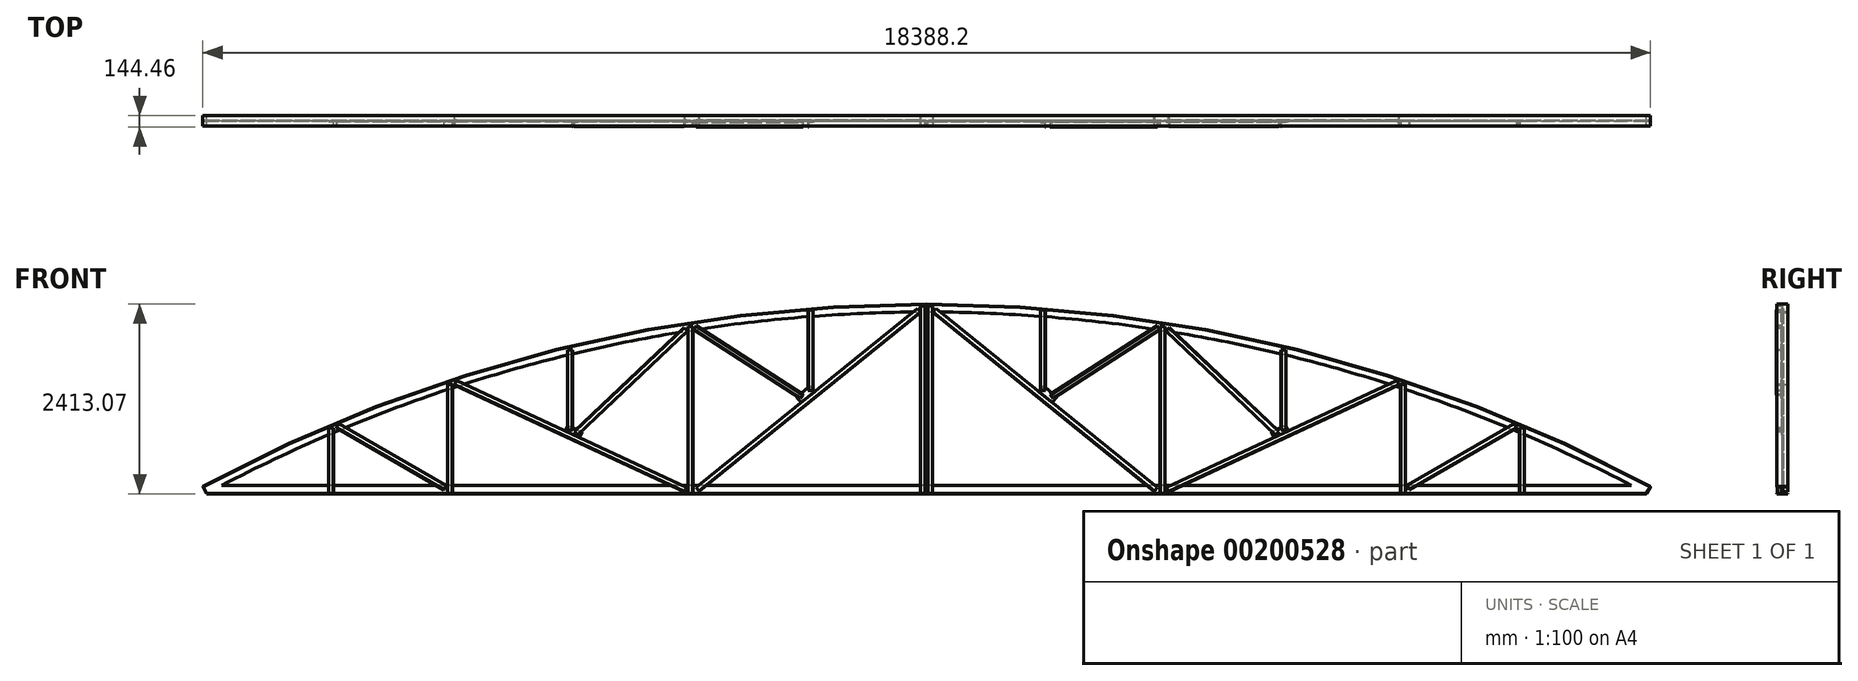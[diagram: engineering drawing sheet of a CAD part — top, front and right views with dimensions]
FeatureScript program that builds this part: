
annotation { "Feature Type Name" : "Feature", "Feature Type Description" : "" }
export const myFeature = defineFeature(function(context is Context, id is Id, definition is map)
    precondition{}
    {
        {
            var Q0;
            Q0=qCreatedBy(makeId("Front.planeOp"),FACE);
            var sketch = newSketch(context, id + "F0", { "sketchPlane" : qUnion([Q0])});
            skLineSegment(sketch, "E0", {"start": v(0, 0) * mm, "end": v(18288, 0) * mm});
            skArc(sketch, "E1", {"start": v(18288, 0) * mm, "mid": v(9144, 2305.05) * mm, "end": v(0, 0) * mm});
            skLineSegment(sketch, "E2", {"start": v(1612.9, 0) * mm, "end": v(1612.9, 774.13) * mm});
            skLineSegment(sketch, "E3", {"start": v(3092.45, 0) * mm, "end": v(3092.45, 1331.2) * mm});
            skLineSegment(sketch, "E4", {"start": v(6115.05, 0) * mm, "end": v(6115.05, 2065.75) * mm});
            skLineSegment(sketch, "E5", {"start": v(9144, 0) * mm, "end": v(9144, 2305.05) * mm});
            skLineSegment(sketch, "E6", {"start": v(7629.52, 1223.6) * mm, "end": v(7629.52, 2245.5) * mm});
            skLineSegment(sketch, "E7", {"start": v(3092.45, 0) * mm, "end": v(1692.88, 807.83) * mm});
            skLineSegment(sketch, "E8", {"start": v(6115.05, 0) * mm, "end": v(3187.59, 1362.37) * mm});
            skLineSegment(sketch, "E9", {"start": v(4651.32, 681.18) * mm, "end": v(4651.32, 1774.56) * mm});
            skLineSegment(sketch, "E10", {"start": v(4651.32, 681.18) * mm, "end": v(6115.05, 2065.75) * mm});
            skLineSegment(sketch, "E11", {"start": v(6190.76, 2077.64) * mm, "end": v(7580.54, 1184.02) * mm});
            skLineSegment(sketch, "E12.MirrorCS", {"start": v(12172.95, 0) * mm, "end": v(9144, 2305.05) * mm});
            skLineSegment(sketch, "E13.MirrorCS", {"start": v(10658.47, 1152.53) * mm, "end": v(10658.47, 2245.5) * mm});
            skLineSegment(sketch, "E14.MirrorCS", {"start": v(12097.24, 2077.64) * mm, "end": v(10658.47, 1152.52) * mm});
            skLineSegment(sketch, "E15.MirrorCS", {"start": v(12172.95, 0) * mm, "end": v(12172.95, 2065.75) * mm});
            skLineSegment(sketch, "E16.MirrorCS", {"start": v(13636.68, 681.18) * mm, "end": v(12172.95, 2065.75) * mm});
            skLineSegment(sketch, "E17.MirrorCS", {"start": v(13636.68, 681.18) * mm, "end": v(13636.68, 1774.56) * mm});
            skLineSegment(sketch, "E18.MirrorCS", {"start": v(12172.95, 0) * mm, "end": v(15100.41, 1362.37) * mm});
            skLineSegment(sketch, "E19.MirrorCS", {"start": v(15195.55, 0) * mm, "end": v(15195.55, 1331.2) * mm});
            skLineSegment(sketch, "E20.MirrorCS", {"start": v(15195.55, 0) * mm, "end": v(16595.12, 807.83) * mm});
            skLineSegment(sketch, "E21.MirrorCS", {"start": v(16675.1, 0) * mm, "end": v(16675.1, 774.13) * mm});
            skLineSegment(sketch, "E22", {"start": v(6115.05, 0) * mm, "end": v(8967.06, 2304.24) * mm});
            skPoint(sketch, "E23.end.orphan", {"position": v(7629.52, 1152.53) * mm});
            skSolve(sketch);
        }
        {
            var Q0;
            Q0=qCreatedBy(makeId("Right.planeOp"),FACE);
            var sketch = newSketch(context, id + "F1", { "sketchPlane" : qUnion([Q0])});
            skLineSegment(sketch, "E24.bottom", {"start": v(-68.26, -3.18) * mm, "end": v(68.26, -3.18) * mm});
            skLineSegment(sketch, "E24.top", {"start": v(-68.26, 3.18) * mm, "end": v(-3.17, 3.18) * mm});
            skLineSegment(sketch, "E24.left", {"start": v(-68.26, -3.18) * mm, "end": v(-68.26, 3.18) * mm});
            skLineSegment(sketch, "E24.right", {"start": v(68.26, -3.18) * mm, "end": v(68.26, 3.18) * mm});
            skPoint(sketch, "E24.middle", {"position": v(0, 0) * mm});
            skLineSegment(sketch, "E25.top", {"start": v(-3.18, 104.78) * mm, "end": v(3.17, 104.78) * mm});
            skLineSegment(sketch, "E25.left", {"start": v(-3.17, 3.18) * mm, "end": v(-3.18, 104.78) * mm});
            skLineSegment(sketch, "E25.right", {"start": v(3.18, 3.18) * mm, "end": v(3.17, 104.78) * mm});
            skLineSegment(sketch, "E26.trimOffspring", {"start": v(3.17, 3.18) * mm, "end": v(68.26, 3.18) * mm});
            skSolve(sketch);
        }
        {
            var Q0;
            Q0 = qSketchRegion(id + "F1", true);
            var Q1;
            Q1=sQuery(id+"F0.wireOp",VERTEX,"E1.start");
            extrude(context, id + "F2", {"entities" : qUnion([Q0]), "endBound" : BoundingType.UP_TO_VERTEX, "endBoundEntityVertex" : qUnion([Q1]), "depth" : 25.4 * mm});
        }
        {
            var Q0;
            Q0=sQuery(id+"F0.wireOp",EDGE,"E1");
            var Q1;
            Q1=sQuery(id+"F0.wireOp",VERTEX,"E0.start");
            cPlane(context, id + "F3", {"entities" : qUnion([Q0, Q1]), "cplaneType" : CPlaneType.CURVE_POINT, "offset" : 25.4 * mm, "width" : 152.4 * mm, "height" : 152.4 * mm});
        }
        {
            var Q0;
            Q0=qCreatedBy(id+"F3.planeOp",FACE);
            var sketch = newSketch(context, id + "F4", { "sketchPlane" : qUnion([Q0])});
            skPoint(sketch, "E27.middle", {"position": v(0, 0) * mm});
            skLineSegment(sketch, "E28.left", {"start": v(3.18, 3.25) * mm, "end": v(3.17, 98.5) * mm});
            skLineSegment(sketch, "E28.right", {"start": v(-3.17, 3.25) * mm, "end": v(-3.18, 98.5) * mm});
            skLineSegment(sketch, "E29", {"start": v(-3.17, 3.25) * mm, "end": v(3.18, 3.25) * mm});
            skLineSegment(sketch, "E30", {"start": v(68.26, 104.85) * mm, "end": v(68.26, 98.5) * mm});
            skLineSegment(sketch, "E31", {"start": v(68.26, 98.5) * mm, "end": v(3.17, 98.5) * mm});
            skLineSegment(sketch, "E32", {"start": v(-68.26, 104.85) * mm, "end": v(-68.26, 98.5) * mm});
            skLineSegment(sketch, "E33", {"start": v(-68.26, 98.5) * mm, "end": v(-3.18, 98.5) * mm});
            skPoint(sketch, "E34.0", {"position": v(68.26, -2.8) * mm});
            skPoint(sketch, "E34.1", {"position": v(-68.26, -2.8) * mm});
            skLineSegment(sketch, "E35", {"start": v(-68.26, 104.85) * mm, "end": v(68.26, 104.85) * mm});
            skSolve(sketch);
        }
        {
            var Q0;
            Q0=makeQuery(id+"F4.imprint","IMPRINT",FACE,{"disambiguationData":[TD([[makeQuery(id+"F4.imprint","IMPRINT",EDGE,{"derivedFrom":sQuery(id+"F4.wireOp",EDGE,"E28.left")}),1.0]])]});
            var Q1;
            Q1=sQuery(id+"F0.wireOp",EDGE,"E1");
            sweep(context, id + "F5", {"profiles" : qUnion([Q0]), "path" : qUnion([Q1])});
        }
        {
            var Q0;
            Q0=sQuery(id+"F0.wireOp",EDGE,"E2");
            var Q1;
            Q1=sQuery(id+"F0.wireOp",VERTEX,"E2.start");
            cPlane(context, id + "F6", {"entities" : qUnion([Q0, Q1]), "cplaneType" : CPlaneType.CURVE_POINT, "offset" : 25.4 * mm, "width" : 152.4 * mm, "height" : 152.4 * mm});
        }
        {
            var Q0;
            Q0=qCreatedBy(id+"F6.planeOp",FACE);
            var sketch = newSketch(context, id + "F7", { "sketchPlane" : qUnion([Q0])});
            skLineSegment(sketch, "E36", {"start": v(1612.9, -66.68) * mm, "end": v(1606.55, -66.68) * mm});
            skLineSegment(sketch, "E37", {"start": v(1606.55, -66.68) * mm, "end": v(1606.55, -9.53) * mm});
            skPoint(sketch, "E38.bottom.start.orphan", {"position": v(1606.55, 0) * mm});
            skLineSegment(sketch, "E39", {"start": v(1612.9, -3.17) * mm, "end": v(1612.9, -66.68) * mm});
            skPoint(sketch, "E40.0", {"position": v(1612.9, 0) * mm});
            skLineSegment(sketch, "E41", {"start": v(1606.55, -9.53) * mm, "end": v(1549.4, -9.53) * mm});
            skLineSegment(sketch, "E42", {"start": v(1549.4, 0) * mm, "end": v(1612.9, 0) * mm});
            skLineSegment(sketch, "E43", {"start": v(1549.4, -3.18) * mm, "end": v(1612.9, -3.17) * mm});
            skPoint(sketch, "E44.start.orphan", {"position": v(1549.4, -6.35) * mm});
            skLineSegment(sketch, "E45", {"start": v(1549.4, -9.53) * mm, "end": v(1549.4, -3.18) * mm});
            skSolve(sketch);
        }
        {
            var Q0;
            Q0 = qSketchRegion(id + "F7", true);
            extrude(context, id + "F8", {"entities" : qUnion([Q0]), "operationType" : NewBodyOperationType.ADD, "depth" : 838.2 * mm});
        }
        {
            var Q0;
            Q0=sQuery(id+"F0.wireOp",EDGE,"E7");
            var Q1;
            Q1=sQuery(id+"F0.wireOp",VERTEX,"E3.start");
            cPlane(context, id + "F9", {"entities" : qUnion([Q0, Q1]), "cplaneType" : CPlaneType.CURVE_POINT, "offset" : 25.4 * mm, "width" : 152.4 * mm, "height" : 152.4 * mm});
        }
        {
            var Q0;
            Q0=qCreatedBy(id+"F9.planeOp",FACE);
            var sketch = newSketch(context, id + "F10", { "sketchPlane" : qUnion([Q0])});
            skPoint(sketch, "E46.0", {"position": v(2.83, 1546.43) * mm});
            skLineSegment(sketch, "E47", {"start": v(3.18, 1545.92) * mm, "end": v(66.67, 1545.92) * mm});
            skLineSegment(sketch, "E48", {"start": v(66.67, 1545.92) * mm, "end": v(66.67, 1552.27) * mm});
            skLineSegment(sketch, "E49", {"start": v(66.67, 1552.27) * mm, "end": v(9.52, 1552.27) * mm});
            skLineSegment(sketch, "E50", {"start": v(9.52, 1552.27) * mm, "end": v(9.52, 1609.42) * mm});
            skLineSegment(sketch, "E51", {"start": v(9.52, 1609.42) * mm, "end": v(3.17, 1609.42) * mm});
            skLineSegment(sketch, "E52", {"start": v(3.17, 1609.42) * mm, "end": v(3.17, 1545.92) * mm});
            skSolve(sketch);
        }
        {
            var Q0;
            Q0 = qSketchRegion(id + "F10", true);
            extrude(context, id + "F11", {"entities" : qUnion([Q0]), "depth" : 1574.8 * mm});
        }
        {
            var Q0;
            Q0=sQuery(id+"F0.wireOp",EDGE,"E3");
            var Q1;
            Q1=sQuery(id+"F0.wireOp",VERTEX,"E7.start");
            cPlane(context, id + "F12", {"entities" : qUnion([Q0, Q1]), "cplaneType" : CPlaneType.CURVE_POINT, "offset" : 25.4 * mm, "width" : 152.4 * mm, "height" : 152.4 * mm});
        }
        {
            var Q0;
            Q0=qCreatedBy(id+"F12.planeOp",FACE);
            var sketch = newSketch(context, id + "F13", { "sketchPlane" : qUnion([Q0])});
            skLineSegment(sketch, "E53", {"start": v(3124.65, -66.68) * mm, "end": v(3124.65, -9.53) * mm});
            skLineSegment(sketch, "E54", {"start": v(3124.65, -66.67) * mm, "end": v(3118.3, -66.67) * mm});
            skLineSegment(sketch, "E55", {"start": v(3118.3, -9.53) * mm, "end": v(3118.3, -66.67) * mm});
            skLineSegment(sketch, "E56", {"start": v(3118.3, -3.17) * mm, "end": v(3061.15, -3.18) * mm});
            skLineSegment(sketch, "E57", {"start": v(3061.15, -3.18) * mm, "end": v(3061.15, -9.53) * mm});
            skLineSegment(sketch, "E58", {"start": v(3061.15, -9.53) * mm, "end": v(3118.3, -9.53) * mm});
            skLineSegment(sketch, "E59", {"start": v(3124.65, -9.53) * mm, "end": v(3124.65, -3.17) * mm});
            skLineSegment(sketch, "E60", {"start": v(3124.65, -3.17) * mm, "end": v(3118.3, -3.17) * mm});
            skSolve(sketch);
        }
        {
            var Q0;
            Q0 = qSketchRegion(id + "F13", true);
            extrude(context, id + "F14", {"entities" : qUnion([Q0]), "depth" : 1386.84 * mm});
        }
        {
            var Q0;
            Q0=makeQuery(id+"F11.opExtrude","SWEPT_BODY",BODY,{"disambiguationData":[OSD([sQuery(id+"F10.wireOp",EDGE,"E47"),sQuery(id+"F10.wireOp",EDGE,"E48"),sQuery(id+"F10.wireOp",EDGE,"E49"),sQuery(id+"F10.wireOp",EDGE,"E50"),sQuery(id+"F10.wireOp",EDGE,"E51"),sQuery(id+"F10.wireOp",EDGE,"E52")])]});
            var Q1;
            Q1=sQuery(id+"F0.wireOp",EDGE,"E7");
            var Q2;
            Q2=sQuery(id+"F0.wireOp",EDGE,"E7");
            transform(context, id + "F15", {"entities" : qUnion([Q0]), "transformType" : TransformType.TRANSLATION_DISTANCE, "transformDirection" : qUnion([Q2]), "distance" : 95.25 * mm, "makeCopy" : false});
        }
        {
            var Q0;
            Q0=sQuery(id+"F0.wireOp",EDGE,"E8");
            var Q1;
            Q1=sQuery(id+"F0.wireOp",VERTEX,"E8.start");
            cPlane(context, id + "F16", {"entities" : qUnion([Q0, Q1]), "cplaneType" : CPlaneType.CURVE_POINT, "offset" : 25.4 * mm, "width" : 152.4 * mm, "height" : 152.4 * mm});
        }
        {
            var Q0;
            Q0=qCreatedBy(id+"F16.planeOp",FACE);
            cPlane(context, id + "F17", {"entities" : qUnion([Q0]), "cplaneType" : CPlaneType.OFFSET, "offset" : 50.8 * mm, "width" : 152.4 * mm, "height" : 152.4 * mm});
        }
        {
            var Q0;
            Q0=qCreatedBy(id+"F17.planeOp",FACE);
            var sketch = newSketch(context, id + "F18", { "sketchPlane" : qUnion([Q0])});
            skPoint(sketch, "E61.0", {"position": v(0, 2580.09) * mm});
            skLineSegment(sketch, "E62.MirrorCS", {"start": v(-3.18, 2580.09) * mm, "end": v(-3.18, 2643.59) * mm});
            skLineSegment(sketch, "E63.MirrorCS", {"start": v(-3.18, 2643.59) * mm, "end": v(-9.53, 2643.59) * mm});
            skLineSegment(sketch, "E64.MirrorCS", {"start": v(-9.53, 2643.59) * mm, "end": v(-9.53, 2586.44) * mm});
            skLineSegment(sketch, "E65.MirrorCS", {"start": v(-9.53, 2586.44) * mm, "end": v(-66.67, 2586.44) * mm});
            skLineSegment(sketch, "E66.MirrorCS", {"start": v(-66.67, 2586.44) * mm, "end": v(-66.67, 2580.09) * mm});
            skLineSegment(sketch, "E67.MirrorCS", {"start": v(-66.67, 2580.09) * mm, "end": v(-3.18, 2580.09) * mm});
            skLineSegment(sketch, "E68.MirrorCS", {"start": v(3.18, 2643.59) * mm, "end": v(9.53, 2643.59) * mm});
            skLineSegment(sketch, "E69.MirrorCS", {"start": v(66.67, 2586.44) * mm, "end": v(66.67, 2580.09) * mm});
            skLineSegment(sketch, "E70.MirrorCS", {"start": v(66.67, 2580.09) * mm, "end": v(3.18, 2580.09) * mm});
            skLineSegment(sketch, "E71.MirrorCS", {"start": v(3.18, 2580.09) * mm, "end": v(3.18, 2643.59) * mm});
            skLineSegment(sketch, "E72.MirrorCS", {"start": v(9.53, 2586.44) * mm, "end": v(66.67, 2586.44) * mm});
            skLineSegment(sketch, "E73.MirrorCS", {"start": v(9.53, 2643.59) * mm, "end": v(9.53, 2586.44) * mm});
            skSolve(sketch);
        }
        {
            var Q0;
            Q0 = qSketchRegion(id + "F18", true);
            extrude(context, id + "F19", {"entities" : qUnion([Q0]), "depth" : 3225.8 * mm});
        }
        {
            var Q0;
            Q0=sQuery(id+"F0.wireOp",EDGE,"E8");
            cPoint(context, id + "F20", {"entities" : qUnion([Q0]), "parameter" : 0.5});
        }
        {
            var Q0;
            Q0=sQuery(id+"F0.wireOp",EDGE,"E9");
            var Q1;
            Q1 = qCreatedBy(id + "F20" ,VERTEX);
            cPlane(context, id + "F21", {"entities" : qUnion([Q0, Q1]), "cplaneType" : CPlaneType.CURVE_POINT, "offset" : 25.4 * mm, "width" : 152.4 * mm, "height" : 152.4 * mm});
        }
        {
            var Q0;
            Q0=qCreatedBy(id+"F21.planeOp",FACE);
            cPlane(context, id + "F22", {"entities" : qUnion([Q0]), "cplaneType" : CPlaneType.OFFSET, "offset" : 127 * mm, "width" : 152.4 * mm, "height" : 152.4 * mm});
        }
        {
            var Q0;
            Q0=qCreatedBy(id+"F22.planeOp",FACE);
            var sketch = newSketch(context, id + "F23", { "sketchPlane" : qUnion([Q0])});
            skLineSegment(sketch, "E74", {"start": v(4644.56, -9.53) * mm, "end": v(4644.56, -73.03) * mm});
            skLineSegment(sketch, "E75", {"start": v(4644.56, -73.03) * mm, "end": v(4638.21, -73.03) * mm});
            skLineSegment(sketch, "E76", {"start": v(4638.21, -73.03) * mm, "end": v(4638.21, -15.88) * mm});
            skLineSegment(sketch, "E77", {"start": v(4638.21, -15.88) * mm, "end": v(4581.06, -15.88) * mm});
            skLineSegment(sketch, "E78", {"start": v(4581.06, -15.88) * mm, "end": v(4581.06, -9.53) * mm});
            skLineSegment(sketch, "E79", {"start": v(4581.06, -9.53) * mm, "end": v(4644.56, -9.53) * mm});
            skLineSegment(sketch, "E80.0", {"start": v(3144.76, -9.53) * mm, "end": v(6117.73, -9.53) * mm});
            skSolve(sketch);
        }
        {
            var Q0;
            Q0 = qSketchRegion(id + "F23", true);
            extrude(context, id + "F24", {"entities" : qUnion([Q0]), "operationType" : NewBodyOperationType.ADD, "depth" : 1016 * mm});
        }
        {
            var Q0;
            Q0=sQuery(id+"F0.wireOp",EDGE,"E10");
            var Q1;
            Q1=sQuery(id+"F0.wireOp",VERTEX,"E10.start");
            cPlane(context, id + "F25", {"entities" : qUnion([Q0, Q1]), "cplaneType" : CPlaneType.CURVE_POINT, "offset" : 25.4 * mm, "width" : 152.4 * mm, "height" : 152.4 * mm});
        }
        {
            var Q0;
            Q0=qCreatedBy(id+"F25.planeOp",FACE);
            cPlane(context, id + "F26", {"entities" : qUnion([Q0]), "cplaneType" : CPlaneType.OFFSET, "offset" : 88.9 * mm, "width" : 152.4 * mm, "height" : 152.4 * mm});
        }
        {
            var Q0;
            Q0=qCreatedBy(id+"F26.planeOp",FACE);
            var sketch = newSketch(context, id + "F27", { "sketchPlane" : qUnion([Q0])});
            skLineSegment(sketch, "E81.0", {"start": v(0.48, -1133.42) * mm, "end": v(0.48, -4181.53) * mm});
            skLineSegment(sketch, "E82", {"start": v(-9.05, -2695.12) * mm, "end": v(-9.05, -2631.62) * mm});
            skLineSegment(sketch, "E83", {"start": v(-9.05, -2631.62) * mm, "end": v(-72.55, -2631.62) * mm});
            skLineSegment(sketch, "E84", {"start": v(-72.55, -2631.62) * mm, "end": v(-72.55, -2637.97) * mm});
            skLineSegment(sketch, "E85", {"start": v(-72.55, -2637.97) * mm, "end": v(-15.4, -2637.97) * mm});
            skLineSegment(sketch, "E86", {"start": v(-15.4, -2637.97) * mm, "end": v(-15.4, -2695.12) * mm});
            skLineSegment(sketch, "E87", {"start": v(-15.4, -2695.12) * mm, "end": v(-9.05, -2695.12) * mm});
            skPoint(sketch, "E88.end.orphan", {"position": v(13.18, -2683.97) * mm});
            skSolve(sketch);
        }
        {
            var Q0;
            Q0 = qSketchRegion(id + "F27", true);
            extrude(context, id + "F28", {"entities" : qUnion([Q0]), "depth" : 1917.7 * mm});
        }
        {
            var Q0;
            Q0=makeQuery(id+"F19.opExtrude","SWEPT_FACE",FACE,{"disambiguationData":[OSD([sQuery(id+"F18.wireOp",EDGE,"E68.MirrorCS")])]});
            var sketch = newSketch(context, id + "F29", { "sketchPlane" : qUnion([Q0])});
            skLineSegment(sketch, "E89.bottom", {"start": v(3789.84, -9.53) * mm, "end": v(3993.04, -9.53) * mm});
            skLineSegment(sketch, "E89.top", {"start": v(3789.84, -3.17) * mm, "end": v(3993.04, -3.17) * mm});
            skLineSegment(sketch, "E89.left", {"start": v(3789.84, -9.53) * mm, "end": v(3789.84, -3.17) * mm});
            skLineSegment(sketch, "E89.right", {"start": v(3993.04, -9.53) * mm, "end": v(3993.04, -3.17) * mm});
            skSolve(sketch);
        }
        {
            var Q0;
            Q0 = qSketchRegion(id + "F29", true);
            extrude(context, id + "F30", {"entities" : qUnion([Q0]), "depth" : 76.96 * mm});
        }
        {
            var Q0;
            Q0=makeQuery(id+"F2.opExtrude","SWEPT_FACE",FACE,{"disambiguationData":[OSD([sQuery(id+"F1.wireOp",EDGE,"E24.top")])]});
            cPlane(context, id + "F31", {"entities" : qUnion([Q0]), "cplaneType" : CPlaneType.OFFSET, "offset" : 0 * mm, "width" : 152.4 * mm, "height" : 152.4 * mm});
        }
        {
            var Q0;
            Q0=qCreatedBy(id+"F31.planeOp",FACE);
            var sketch = newSketch(context, id + "F32", { "sketchPlane" : qUnion([Q0])});
            skPoint(sketch, "E90.0", {"position": v(6115.05, 0) * mm});
            skLineSegment(sketch, "E91", {"start": v(6115.05, -3.18) * mm, "end": v(6178.55, -3.18) * mm});
            skLineSegment(sketch, "E92", {"start": v(6178.55, -3.18) * mm, "end": v(6178.55, -9.53) * mm});
            skLineSegment(sketch, "E93", {"start": v(6115.05, -9.53) * mm, "end": v(6115.05, -3.17) * mm});
            skLineSegment(sketch, "E94", {"start": v(6178.55, -9.53) * mm, "end": v(6178.55, -66.67) * mm});
            skLineSegment(sketch, "E95", {"start": v(6178.55, -66.67) * mm, "end": v(6172.2, -66.67) * mm});
            skLineSegment(sketch, "E96", {"start": v(6172.2, -66.67) * mm, "end": v(6172.2, -9.53) * mm});
            skPoint(sketch, "E97.start.orphan", {"position": v(6122.79, -66.68) * mm});
            skPoint(sketch, "E98.orphan", {"position": v(6115.05, -66.67) * mm});
            skLineSegment(sketch, "E99", {"start": v(6115.05, -9.53) * mm, "end": v(6172.2, -9.53) * mm});
            skSolve(sketch);
        }
        {
            var Q0;
            Q0 = qSketchRegion(id + "F32", true);
            extrude(context, id + "F33", {"entities" : qUnion([Q0]), "depth" : 2120.9 * mm});
        }
        {
            var Q0;
            Q0=makeQuery(id+"F2.opExtrude","SWEPT_FACE",FACE,{"disambiguationData":[OSD([sQuery(id+"F1.wireOp",EDGE,"E24.top")])]});
            var sketch = newSketch(context, id + "F34", { "sketchPlane" : qUnion([Q0])});
            skPoint(sketch, "E100.0", {"position": v(9144, 0) * mm});
            skLineSegment(sketch, "E101.0", {"start": v(0, 0) * mm, "end": v(18288, 0) * mm});
            skLineSegment(sketch, "E102", {"start": v(9131.7, -3.17) * mm, "end": v(9131.7, -66.67) * mm});
            skLineSegment(sketch, "E103", {"start": v(9131.7, -66.67) * mm, "end": v(9125.35, -66.67) * mm});
            skLineSegment(sketch, "E104", {"start": v(9125.35, -66.67) * mm, "end": v(9125.35, -9.52) * mm});
            skLineSegment(sketch, "E105", {"start": v(9125.35, -9.52) * mm, "end": v(9068.2, -9.53) * mm});
            skLineSegment(sketch, "E106", {"start": v(9068.2, -9.53) * mm, "end": v(9068.2, -3.18) * mm});
            skLineSegment(sketch, "E107", {"start": v(9068.2, -3.17) * mm, "end": v(9131.7, -3.17) * mm});
            skSolve(sketch);
        }
        {
            var Q0;
            Q0=makeQuery(id+"F34.imprint","IMPRINT",FACE,{"disambiguationData":[TD([[makeQuery(id+"F34.imprint","IMPRINT",EDGE,{"derivedFrom":sQuery(id+"F34.wireOp",EDGE,"E102")}),-1.0]])]});
            extrude(context, id + "F35", {"entities" : qUnion([Q0]), "operationType" : NewBodyOperationType.ADD, "depth" : 2379.98 * mm});
        }
        {
            var Q0;
            Q0=sQuery(id+"F0.wireOp",EDGE,"E22");
            var Q1;
            Q1=sQuery(id+"F0.wireOp",VERTEX,"E4.start");
            cPlane(context, id + "F36", {"entities" : qUnion([Q0, Q1]), "cplaneType" : CPlaneType.CURVE_POINT, "offset" : 25.4 * mm, "width" : 152.4 * mm, "height" : 152.4 * mm});
        }
        {
            var Q0;
            Q0=qCreatedBy(id+"F36.planeOp",FACE);
            cPlane(context, id + "F37", {"entities" : qUnion([Q0]), "cplaneType" : CPlaneType.OFFSET, "offset" : 129.54 * mm, "width" : 152.4 * mm, "height" : 152.4 * mm});
        }
        {
            var Q0;
            Q0=qCreatedBy(id+"F37.planeOp",FACE);
            var sketch = newSketch(context, id + "F38", { "sketchPlane" : qUnion([Q0])});
            skPoint(sketch, "E108.0", {"position": v(0, -3843) * mm});
            skLineSegment(sketch, "E109", {"start": v(0, -3843) * mm, "end": v(-4.09, -3843) * mm});
            skLineSegment(sketch, "E110", {"start": v(-4.09, -3843) * mm, "end": v(-4.09, -3906.5) * mm});
            skLineSegment(sketch, "E111", {"start": v(-4.09, -3906.5) * mm, "end": v(-67.59, -3906.5) * mm});
            skLineSegment(sketch, "E112", {"start": v(-67.59, -3906.5) * mm, "end": v(-67.59, -3900.16) * mm});
            skLineSegment(sketch, "E113", {"start": v(-67.59, -3900.16) * mm, "end": v(-10.44, -3900.16) * mm});
            skLineSegment(sketch, "E114", {"start": v(-10.44, -3900.16) * mm, "end": v(-10.44, -3843) * mm});
            skLineSegment(sketch, "E115", {"start": v(-10.44, -3843) * mm, "end": v(-4.09, -3843) * mm});
            skLineSegment(sketch, "E116.MirrorCS", {"start": v(4.09, -3843) * mm, "end": v(4.09, -3906.5) * mm});
            skLineSegment(sketch, "E117.MirrorCS", {"start": v(10.44, -3900.16) * mm, "end": v(10.44, -3843) * mm});
            skLineSegment(sketch, "E118.MirrorCS", {"start": v(67.59, -3900.16) * mm, "end": v(10.44, -3900.16) * mm});
            skLineSegment(sketch, "E119.MirrorCS", {"start": v(10.44, -3843) * mm, "end": v(4.09, -3843) * mm});
            skLineSegment(sketch, "E120.MirrorCS", {"start": v(4.09, -3906.5) * mm, "end": v(67.59, -3906.5) * mm});
            skLineSegment(sketch, "E121.MirrorCS", {"start": v(67.59, -3906.5) * mm, "end": v(67.59, -3900.16) * mm});
            skSolve(sketch);
        }
        {
            var Q0;
            Q0 = qSketchRegion(id + "F38", true);
            extrude(context, id + "F39", {"entities" : qUnion([Q0]), "depth" : 3614.42 * mm});
        }
        {
            var Q0;
            Q0=sQuery(id+"F0.wireOp",EDGE,"E6");
            var Q1;
            Q1=sQuery(id+"F0.wireOp",VERTEX,"E23.end.orphan");
            cPlane(context, id + "F40", {"entities" : qUnion([Q0, Q1]), "cplaneType" : CPlaneType.CURVE_POINT, "offset" : 25.4 * mm, "width" : 152.4 * mm, "height" : 152.4 * mm});
        }
        {
            var Q0;
            Q0=qCreatedBy(id+"F40.planeOp",FACE);
            cPlane(context, id + "F41", {"entities" : qUnion([Q0]), "cplaneType" : CPlaneType.OFFSET, "offset" : 157.48 * mm, "width" : 152.4 * mm, "height" : 152.4 * mm});
        }
        {
            var Q0;
            Q0=qCreatedBy(id+"F41.planeOp",FACE);
            var sketch = newSketch(context, id + "F42", { "sketchPlane" : qUnion([Q0])});
            skLineSegment(sketch, "E122", {"start": v(7638.44, -76.2) * mm, "end": v(7638.44, -12.7) * mm});
            skLineSegment(sketch, "E123", {"start": v(7638.44, -76.2) * mm, "end": v(7644.79, -76.2) * mm});
            skLineSegment(sketch, "E124", {"start": v(7644.79, -19.05) * mm, "end": v(7644.79, -76.2) * mm});
            skLineSegment(sketch, "E125", {"start": v(7701.94, 0) * mm, "end": v(7638.44, 0) * mm});
            skLineSegment(sketch, "E126", {"start": v(7638.44, 0) * mm, "end": v(7701.94, 0) * mm});
            skPoint(sketch, "E127.0", {"position": v(7629.52, 0) * mm});
            skLineSegment(sketch, "E128", {"start": v(7701.94, -19.05) * mm, "end": v(7644.79, -19.05) * mm});
            skLineSegment(sketch, "E129", {"start": v(7701.94, -12.7) * mm, "end": v(7701.94, -19.05) * mm});
            skLineSegment(sketch, "E130", {"start": v(7638.44, -12.7) * mm, "end": v(7701.94, -12.7) * mm});
            skSolve(sketch);
        }
        {
            var Q0;
            Q0 = qSketchRegion(id + "F42", true);
            extrude(context, id + "F43", {"entities" : qUnion([Q0]), "operationType" : NewBodyOperationType.ADD, "depth" : 1021.08 * mm});
        }
        {
            var Q0;
            Q0=sQuery(id+"F0.wireOp",EDGE,"E11");
            var Q1;
            Q1=sQuery(id+"F0.wireOp",VERTEX,"E23.end.orphan");
            cPlane(context, id + "F44", {"entities" : qUnion([Q0, Q1]), "cplaneType" : CPlaneType.CURVE_POINT, "offset" : 25.4 * mm, "width" : 152.4 * mm, "height" : 152.4 * mm});
        }
        {
            var Q0;
            Q0=qCreatedBy(id+"F44.planeOp",FACE);
            cPlane(context, id + "F45", {"entities" : qUnion([Q0]), "cplaneType" : CPlaneType.OFFSET, "offset" : 104.14 * mm, "oppositeDirection" : true, "width" : 152.4 * mm, "height" : 152.4 * mm});
        }
        {
            var Q0;
            Q0=qCreatedBy(id+"F45.planeOp",FACE);
            var sketch = newSketch(context, id + "F46", { "sketchPlane" : qUnion([Q0])});
            skLineSegment(sketch, "E131.0.1", {"start": v(0, 5095.74) * mm, "end": v(0, 5155.52) * mm});
            skLineSegment(sketch, "E131.0.2", {"start": v(0, 5155.52) * mm, "end": v(0, 6015.07) * mm});
            skLineSegment(sketch, "E131.0.3", {"start": v(0, 6015.07) * mm, "end": v(0, 5095.74) * mm});
            skLineSegment(sketch, "E132", {"start": v(-12.7, 5159.52) * mm, "end": v(-76.2, 5159.52) * mm});
            skLineSegment(sketch, "E133", {"start": v(-76.2, 5159.52) * mm, "end": v(-76.2, 5153.17) * mm});
            skLineSegment(sketch, "E134", {"start": v(-76.2, 5153.17) * mm, "end": v(-19.05, 5153.17) * mm});
            skLineSegment(sketch, "E135", {"start": v(-19.05, 5153.17) * mm, "end": v(-19.05, 5096.15) * mm});
            skLineSegment(sketch, "E136", {"start": v(-19.05, 5096.15) * mm, "end": v(-12.7, 5096.02) * mm});
            skLineSegment(sketch, "E137", {"start": v(0, 5159.52) * mm, "end": v(0, 5095.74) * mm});
            skLineSegment(sketch, "E138", {"start": v(-12.7, 5096.02) * mm, "end": v(-12.7, 5159.52) * mm});
            skSolve(sketch);
        }
        {
            var Q0;
            Q0 = qSketchRegion(id + "F46", true);
            extrude(context, id + "F47", {"entities" : qUnion([Q0]), "operationType" : NewBodyOperationType.ADD, "oppositeDirection" : true, "depth" : 1617.98 * mm});
        }
        {
            var Q0;
            Q0=makeQuery(id+"F39.opExtrude","SWEPT_FACE",FACE,{"disambiguationData":[OSD([sQuery(id+"F38.wireOp",EDGE,"E115")])]});
            var sketch = newSketch(context, id + "F48", { "sketchPlane" : qUnion([Q0])});
            skLineSegment(sketch, "E139.bottom", {"start": v(6601.21, -10.44) * mm, "end": v(6817.11, -10.44) * mm});
            skLineSegment(sketch, "E139.top", {"start": v(6601.21, -4.09) * mm, "end": v(6817.11, -4.09) * mm});
            skLineSegment(sketch, "E139.left", {"start": v(6601.21, -10.44) * mm, "end": v(6601.21, -4.09) * mm});
            skLineSegment(sketch, "E139.right", {"start": v(6817.11, -10.44) * mm, "end": v(6817.11, -4.09) * mm});
            skSolve(sketch);
        }
        {
            var Q0;
            Q0 = qSketchRegion(id + "F48", true);
            extrude(context, id + "F49", {"entities" : qUnion([Q0]), "depth" : 91.44 * mm});
        }
        {
            var Q0;
            Q0=makeQuery(id+"F35.opExtrude","SWEPT_FACE",FACE,{"disambiguationData":[OSD([sQuery(id+"F34.wireOp",EDGE,"E102")])]});
            cPlane(context, id + "F50", {"entities" : qUnion([Q0]), "cplaneType" : CPlaneType.OFFSET, "offset" : 12.7 * mm, "width" : 152.4 * mm, "height" : 152.4 * mm});
        }
        {
            var Q0;
            Q0=makeQuery(id+"F39.opExtrude","SWEPT_BODY",BODY,{"disambiguationData":[OSD([sQuery(id+"F38.wireOp",EDGE,"E110"),sQuery(id+"F38.wireOp",EDGE,"E111"),sQuery(id+"F38.wireOp",EDGE,"E112"),sQuery(id+"F38.wireOp",EDGE,"E113"),sQuery(id+"F38.wireOp",EDGE,"E114"),sQuery(id+"F38.wireOp",EDGE,"E115")])]});
            var Q1;
            Q1=makeQuery(id+"F43.opExtrude","SWEPT_BODY",BODY,{"disambiguationData":[OSD([sQuery(id+"F42.wireOp",EDGE,"E122"),sQuery(id+"F42.wireOp",EDGE,"E123"),sQuery(id+"F42.wireOp",EDGE,"E124"),sQuery(id+"F42.wireOp",EDGE,"uOuj5NGx-17GM-Mw7A-FTPI-DWF7fpRwAIm5"),sQuery(id+"F42.wireOp",EDGE,"dZkJSmds-j7UH-SSCP-u4Ih-RMBNkNQA11X7"),sQuery(id+"F42.wireOp",EDGE,"E126")])]});
            var Q2;
            Q2=makeQuery(id+"F49.opExtrude","SWEPT_BODY",BODY,{"disambiguationData":[OSD([sQuery(id+"F48.wireOp",EDGE,"E139.bottom"),sQuery(id+"F48.wireOp",EDGE,"E139.top"),sQuery(id+"F48.wireOp",EDGE,"E139.left"),sQuery(id+"F48.wireOp",EDGE,"E139.right")])]});
            var Q3;
            Q3=makeQuery(id+"F5.opSweep","SWEPT_BODY",BODY,{"disambiguationData":[OSD([sQuery(id+"F0.wireOp",EDGE,"E1"),sQuery(id+"F4.wireOp",EDGE,"E28.left"),sQuery(id+"F4.wireOp",EDGE,"E28.right"),sQuery(id+"F4.wireOp",EDGE,"E29"),sQuery(id+"F4.wireOp",EDGE,"E30"),sQuery(id+"F4.wireOp",EDGE,"E31"),sQuery(id+"F4.wireOp",EDGE,"E32"),sQuery(id+"F4.wireOp",EDGE,"E33"),sQuery(id+"F4.wireOp",EDGE,"E35")])]});
            var Q4;
            Q4=makeQuery(id+"F33.opExtrude","SWEPT_BODY",BODY,{"disambiguationData":[OSD([sQuery(id+"F32.wireOp",EDGE,"E91"),sQuery(id+"F32.wireOp",EDGE,"E92"),sQuery(id+"F32.wireOp",EDGE,"E93"),sQuery(id+"F32.wireOp",EDGE,"E94"),sQuery(id+"F32.wireOp",EDGE,"E95"),sQuery(id+"F32.wireOp",EDGE,"E96"),sQuery(id+"F32.wireOp",EDGE,"E99")])]});
            var Q5;
            Q5=makeQuery(id+"F28.opExtrude","SWEPT_BODY",BODY,{"disambiguationData":[OSD([sQuery(id+"F27.wireOp",EDGE,"E82"),sQuery(id+"F27.wireOp",EDGE,"E83"),sQuery(id+"F27.wireOp",EDGE,"E84"),sQuery(id+"F27.wireOp",EDGE,"E85"),sQuery(id+"F27.wireOp",EDGE,"E86"),sQuery(id+"F27.wireOp",EDGE,"E87")])]});
            var Q6;
            Q6=makeQuery(id+"F19.opExtrude","SWEPT_BODY",BODY,{"disambiguationData":[OSD([sQuery(id+"F18.wireOp",EDGE,"fR6K2I5n-3yyS-XcYj-GziI-SimCiqrJYMnS"),sQuery(id+"F18.wireOp",EDGE,"DomAPrI3-vOdW-qizV-5RqZ-W5uNoyG2PKUz"),sQuery(id+"F18.wireOp",EDGE,"gMHwrGF1-JGd2-y6CO-m9wL-YWMoOy4B9Btv"),sQuery(id+"F18.wireOp",EDGE,"1H9iAEpe-uR8N-W58M-Nnsx-awdP13kMLbvY"),sQuery(id+"F18.wireOp",EDGE,"WdFXNTIy-uckv-oNBa-KU6S-SmvUdIfRYj6D"),sQuery(id+"F18.wireOp",EDGE,"QOBKChic-byfR-FNSD-CDCA-rWGsIW7gaVbq")])]});
            var Q7;
            Q7=makeQuery(id+"F24.opExtrude","SWEPT_BODY",BODY,{"disambiguationData":[OSD([sQuery(id+"F23.wireOp",EDGE,"E74"),sQuery(id+"F23.wireOp",EDGE,"E75"),sQuery(id+"F23.wireOp",EDGE,"E76"),sQuery(id+"F23.wireOp",EDGE,"E77"),sQuery(id+"F23.wireOp",EDGE,"E78"),sQuery(id+"F23.wireOp",EDGE,"E80.0")])]});
            var Q8;
            Q8=makeQuery(id+"F14.opExtrude","SWEPT_BODY",BODY,{"disambiguationData":[OSD([sQuery(id+"F13.wireOp",EDGE,"E53"),sQuery(id+"F13.wireOp",EDGE,"E54"),sQuery(id+"F13.wireOp",EDGE,"E55"),sQuery(id+"F13.wireOp",EDGE,"E56"),sQuery(id+"F13.wireOp",EDGE,"E57"),sQuery(id+"F13.wireOp",EDGE,"E58"),sQuery(id+"F13.wireOp",EDGE,"E59"),sQuery(id+"F13.wireOp",EDGE,"E60")])]});
            var Q9;
            Q9=makeQuery(id+"F11.opExtrude","SWEPT_BODY",BODY,{"disambiguationData":[OSD([sQuery(id+"F10.wireOp",EDGE,"E47"),sQuery(id+"F10.wireOp",EDGE,"E48"),sQuery(id+"F10.wireOp",EDGE,"E49"),sQuery(id+"F10.wireOp",EDGE,"E50"),sQuery(id+"F10.wireOp",EDGE,"E51"),sQuery(id+"F10.wireOp",EDGE,"E52")])]});
            var Q10;
            Q10=makeQuery(id+"F2.opExtrude","SWEPT_BODY",BODY,{"disambiguationData":[OSD([sQuery(id+"F1.wireOp",EDGE,"E24.bottom"),sQuery(id+"F1.wireOp",EDGE,"E24.top"),sQuery(id+"F1.wireOp",EDGE,"E24.left"),sQuery(id+"F1.wireOp",EDGE,"E24.right"),sQuery(id+"F1.wireOp",EDGE,"E25.top"),sQuery(id+"F1.wireOp",EDGE,"E25.left"),sQuery(id+"F1.wireOp",EDGE,"E25.right"),sQuery(id+"F1.wireOp",EDGE,"E26.trimOffspring")])]});
            var Q11;
            Q11=makeQuery(id+"F39.opExtrude","SWEPT_BODY",BODY,{"disambiguationData":[OSD([sQuery(id+"F38.wireOp",EDGE,"E116.MirrorCS"),sQuery(id+"F38.wireOp",EDGE,"E117.MirrorCS"),sQuery(id+"F38.wireOp",EDGE,"E118.MirrorCS"),sQuery(id+"F38.wireOp",EDGE,"E119.MirrorCS"),sQuery(id+"F38.wireOp",EDGE,"E120.MirrorCS"),sQuery(id+"F38.wireOp",EDGE,"E121.MirrorCS")])]});
            var Q12;
            Q12=makeQuery(id+"F19.opExtrude","SWEPT_BODY",BODY,{"disambiguationData":[OSD([sQuery(id+"F18.wireOp",EDGE,"E62.MirrorCS"),sQuery(id+"F18.wireOp",EDGE,"E63.MirrorCS"),sQuery(id+"F18.wireOp",EDGE,"E64.MirrorCS"),sQuery(id+"F18.wireOp",EDGE,"E65.MirrorCS"),sQuery(id+"F18.wireOp",EDGE,"E66.MirrorCS"),sQuery(id+"F18.wireOp",EDGE,"E67.MirrorCS")])]});
            var Q13;
            Q13=makeQuery(id+"F30.opExtrude","SWEPT_BODY",BODY,{"disambiguationData":[OSD([sQuery(id+"F29.wireOp",EDGE,"E89.bottom"),sQuery(id+"F29.wireOp",EDGE,"E89.top"),sQuery(id+"F29.wireOp",EDGE,"E89.left"),sQuery(id+"F29.wireOp",EDGE,"E89.right")])]});
            var Q14;
            Q14=makeQuery(id+"F47.opExtrude","SWEPT_BODY",BODY,{"disambiguationData":[OSD([sQuery(id+"F46.wireOp",EDGE,"E132"),sQuery(id+"F46.wireOp",EDGE,"E133"),sQuery(id+"F46.wireOp",EDGE,"E134"),sQuery(id+"F46.wireOp",EDGE,"E135"),sQuery(id+"F46.wireOp",EDGE,"E136"),sQuery(id+"F46.wireOp",EDGE,"E138")])]});
            var Q15;
            Q15=makeQuery(id+"F19.opExtrude","SWEPT_BODY",BODY,{"disambiguationData":[OSD([sQuery(id+"F18.wireOp",EDGE,"E68.MirrorCS"),sQuery(id+"F18.wireOp",EDGE,"E69.MirrorCS"),sQuery(id+"F18.wireOp",EDGE,"E70.MirrorCS"),sQuery(id+"F18.wireOp",EDGE,"E71.MirrorCS"),sQuery(id+"F18.wireOp",EDGE,"E72.MirrorCS"),sQuery(id+"F18.wireOp",EDGE,"E73.MirrorCS")])]});
            var Q16;
            Q16=qCreatedBy(id+"F50.planeOp",FACE);
            mirror(context, id + "F51", {"entities" : qUnion([Q0, Q1, Q2, Q3, Q4, Q5, Q6, Q7, Q8, Q9, Q10, Q11, Q12, Q13, Q14, Q15]), "mirrorPlane" : qUnion([Q16])});
        }
    });
